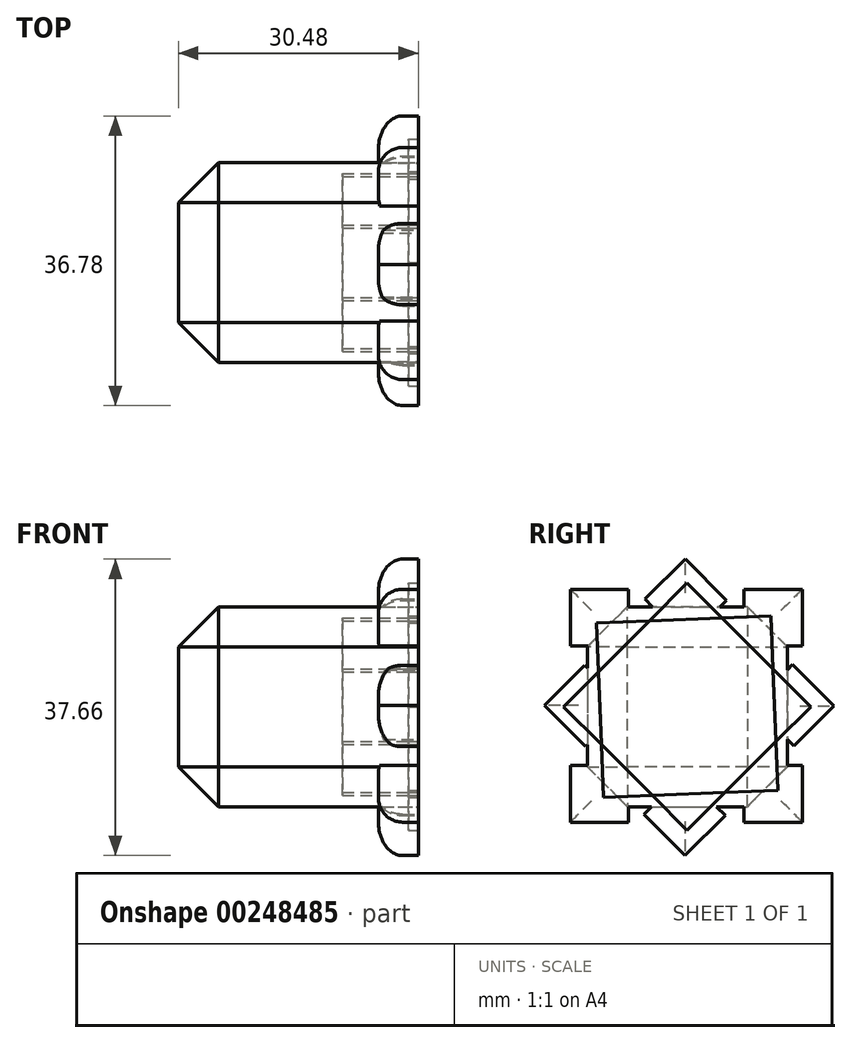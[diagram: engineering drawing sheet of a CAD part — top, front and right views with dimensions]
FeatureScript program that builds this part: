
annotation { "Feature Type Name" : "Feature", "Feature Type Description" : "" }
export const myFeature = defineFeature(function(context is Context, id is Id, definition is map)
    precondition{}
    {
        {
            var Q0;
            Q0=qCreatedBy(makeId("Front.planeOp"),FACE);
            var sketch = newSketch(context, id + "F0", { "sketchPlane" : qUnion([Q0])});
            skLineSegment(sketch, "E0.bottom", {"start": v(12.7, 12.7) * mm, "end": v(-12.7, 12.7) * mm});
            skLineSegment(sketch, "E0.top", {"start": v(12.7, -12.7) * mm, "end": v(-12.7, -12.7) * mm});
            skLineSegment(sketch, "E0.left", {"start": v(12.7, 12.7) * mm, "end": v(12.7, -12.7) * mm});
            skLineSegment(sketch, "E0.right", {"start": v(-12.7, 12.7) * mm, "end": v(-12.7, -12.7) * mm});
            skPoint(sketch, "E0.middle", {"position": v(0, 0) * mm});
            skSolve(sketch);
        }
        {
            var Q0;
            Q0=makeQuery(id+"F0.imprint","IMPRINT",FACE,{"disambiguationData":[TD([[makeQuery(id+"F0.imprint","IMPRINT",EDGE,{"derivedFrom":sQuery(id+"F0.wireOp",EDGE,"E0.bottom")}),1.0]])]});
            extrude(context, id + "F1", {"entities" : qUnion([Q0]), "depth" : 25.4 * mm});
        }
        {
            var Q0;
            Q0=makeQuery(id+"F1.opExtrude","SWEPT_FACE",FACE,{"disambiguationData":[OSD([sQuery(id+"F0.wireOp",EDGE,"E0.left")])]});
            var sketch = newSketch(context, id + "F2", { "sketchPlane" : qUnion([Q0])});
            skLineSegment(sketch, "E1.bottom", {"start": v(-27.56, 7.72) * mm, "end": v(-27.56, 14.93) * mm});
            skLineSegment(sketch, "E1.top", {"start": v(-20.15, 7.72) * mm, "end": v(-20.15, 14.93) * mm});
            skLineSegment(sketch, "E1.left", {"start": v(-27.56, 7.72) * mm, "end": v(-20.15, 7.72) * mm});
            skLineSegment(sketch, "E1.right", {"start": v(-27.56, 14.93) * mm, "end": v(-20.15, 14.93) * mm});
            skLineSegment(sketch, "E2.bottom", {"start": v(-5.5, 7.72) * mm, "end": v(-5.5, 14.93) * mm});
            skLineSegment(sketch, "E2.top", {"start": v(1.9, 7.72) * mm, "end": v(1.9, 14.93) * mm});
            skLineSegment(sketch, "E2.left", {"start": v(-5.5, 7.72) * mm, "end": v(1.9, 7.72) * mm});
            skLineSegment(sketch, "E2.right", {"start": v(-5.5, 14.93) * mm, "end": v(1.9, 14.93) * mm});
            skLineSegment(sketch, "E3.bottom", {"start": v(-5.5, -14.66) * mm, "end": v(-5.5, -7.45) * mm});
            skLineSegment(sketch, "E3.top", {"start": v(1.9, -14.66) * mm, "end": v(1.9, -7.45) * mm});
            skLineSegment(sketch, "E3.left", {"start": v(-5.5, -14.66) * mm, "end": v(1.9, -14.66) * mm});
            skLineSegment(sketch, "E3.right", {"start": v(-5.5, -7.45) * mm, "end": v(1.9, -7.45) * mm});
            skLineSegment(sketch, "E4.bottom", {"start": v(-27.56, -14.66) * mm, "end": v(-27.56, -7.45) * mm});
            skLineSegment(sketch, "E4.left", {"start": v(-27.56, -14.66) * mm, "end": v(-20.15, -14.66) * mm});
            skLineSegment(sketch, "E4.right", {"start": v(-27.56, -7.45) * mm, "end": v(-20.15, -7.45) * mm});
            skPoint(sketch, "E5", {"position": v(-5.5, -11.06) * mm});
            skPoint(sketch, "E6", {"position": v(-23.86, -7.45) * mm});
            skPoint(sketch, "E7", {"position": v(-1.8, -7.45) * mm});
            skPoint(sketch, "E8", {"position": v(-20.15, 11.32) * mm});
            skLineSegment(sketch, "E9", {"start": v(-20.15, -7.45) * mm, "end": v(-20.15, -14.66) * mm});
            skSolve(sketch);
        }
        {
            var Q0;
            {var subQ2=sQuery(id+"F2.wireOp",EDGE,"E1.bottom");Q0=makeQuery(id+"F2.imprint","IMPRINT",FACE,{"disambiguationData":[TD([[makeQuery(id+"F2.imprint","IMPRINT",EDGE,{"derivedFrom":subQ2}),-1.0]])]});}
            var Q1;
            {var subQ0=sQuery(id+"F2.wireOp",EDGE,"E1.left");var subQ1=sQuery(id+"F2.wireOp",EDGE,"E1.top");var subQ2=makeQuery(id+"F2.imprint","INTERSECT",VERTEX,{"derivedFrom":[subQ1,subQ0]});Q1=makeQuery(id+"F2.imprint","IMPRINT",FACE,{"disambiguationData":[TD([[makeQuery(id+"F2.imprint","IMPRINT",EDGE,{"disambiguationData":[TD([[subQ2,1.0]])],"derivedFrom":subQ0}),1.0]])]});}
            var Q2;
            {var subQ0=sQuery(id+"F2.wireOp",EDGE,"E2.left");var subQ1=sQuery(id+"F2.wireOp",EDGE,"E2.bottom");var subQ2=makeQuery(id+"F2.imprint","INTERSECT",VERTEX,{"derivedFrom":[subQ1,subQ0]});Q2=makeQuery(id+"F2.imprint","IMPRINT",FACE,{"disambiguationData":[TD([[makeQuery(id+"F2.imprint","IMPRINT",EDGE,{"disambiguationData":[TD([[subQ2,-1.0]])],"derivedFrom":subQ0}),1.0]])]});}
            var Q3;
            {var subQ7=sQuery(id+"F2.wireOp",EDGE,"E2.top");Q3=makeQuery(id+"F2.imprint","IMPRINT",FACE,{"disambiguationData":[TD([[makeQuery(id+"F2.imprint","IMPRINT",EDGE,{"derivedFrom":subQ7}),1.0]])]});}
            var Q4;
            {var subQ1=sQuery(id+"F2.wireOp",EDGE,"E3.top");Q4=makeQuery(id+"F2.imprint","IMPRINT",FACE,{"disambiguationData":[TD([[makeQuery(id+"F2.imprint","IMPRINT",EDGE,{"derivedFrom":subQ1}),1.0]])]});}
            var Q5;
            {var subQ1=sQuery(id+"F2.wireOp",EDGE,"E4.bottom");Q5=makeQuery(id+"F2.imprint","IMPRINT",FACE,{"disambiguationData":[TD([[makeQuery(id+"F2.imprint","IMPRINT",EDGE,{"derivedFrom":subQ1}),-1.0]])]});}
            var Q6;
            {var subQ0=sQuery(id+"F2.wireOp",EDGE,"E4.right");var subQ1=sQuery(id+"F2.wireOp",EDGE,"E4.top");var subQ2=makeQuery(id+"F2.imprint","INTERSECT",VERTEX,{"derivedFrom":[subQ1,subQ0]});Q6=makeQuery(id+"F2.imprint","IMPRINT",FACE,{"disambiguationData":[TD([[makeQuery(id+"F2.imprint","IMPRINT",EDGE,{"disambiguationData":[TD([[subQ2,1.0]])],"derivedFrom":subQ0}),-1.0]])]});}
            var Q7;
            {var subQ0=sQuery(id+"F2.wireOp",EDGE,"E3.right");var subQ1=sQuery(id+"F2.wireOp",EDGE,"E3.bottom");var subQ2=makeQuery(id+"F2.imprint","INTERSECT",VERTEX,{"derivedFrom":[subQ1,subQ0]});Q7=makeQuery(id+"F2.imprint","IMPRINT",FACE,{"disambiguationData":[TD([[makeQuery(id+"F2.imprint","IMPRINT",EDGE,{"disambiguationData":[TD([[subQ2,-1.0]])],"derivedFrom":subQ0}),-1.0]])]});}
            var Q8;
            Q8=makeQuery(id+"F1.opExtrude","SWEPT_FACE",FACE,{"disambiguationData":[OSD([sQuery(id+"F0.wireOp",EDGE,"E0.left")])]});
            var Q9;
            Q9=makeQuery(id+"F1.opExtrude","SWEPT_FACE",FACE,{"disambiguationData":[OSD([sQuery(id+"F0.wireOp",EDGE,"E0.right")])]});
            extrude(context, id + "F3", {"entities" : qUnion([Q0, Q1, Q2, Q3, Q4, Q5, Q6, Q7, Q8, Q9]), "operationType" : NewBodyOperationType.ADD, "endBound" : BoundingType.SYMMETRIC, "depth" : 5.08 * mm});
        }
        {
            var Q0;
            Q0=makeQuery(id+"F3.boolean.opBoolean","MERGE",FACE,{"derivedFrom":[makeQuery(id+"F3.opExtrude","CAP_FACE",FACE,{"disambiguationData":[OSD([sQuery(id+"F0.wireOp",EDGE,"E0.left")])],"isStart":false}),makeQuery(id+"F3.opExtrude","CAP_FACE",FACE,{"disambiguationData":[OSD([sQuery(id+"F2.wireOp",EDGE,"E1.bottom"),sQuery(id+"F2.wireOp",EDGE,"E1.top"),sQuery(id+"F2.wireOp",EDGE,"E1.left"),sQuery(id+"F2.wireOp",EDGE,"E1.right")])],"isStart":false}),makeQuery(id+"F3.opExtrude","CAP_FACE",FACE,{"disambiguationData":[OSD([sQuery(id+"F2.wireOp",EDGE,"E2.bottom"),sQuery(id+"F2.wireOp",EDGE,"E2.top"),sQuery(id+"F2.wireOp",EDGE,"E2.left"),sQuery(id+"F2.wireOp",EDGE,"E2.right")])],"isStart":false}),makeQuery(id+"F3.opExtrude","CAP_FACE",FACE,{"disambiguationData":[OSD([sQuery(id+"F2.wireOp",EDGE,"E3.bottom"),sQuery(id+"F2.wireOp",EDGE,"E3.top"),sQuery(id+"F2.wireOp",EDGE,"E3.left"),sQuery(id+"F2.wireOp",EDGE,"E3.right")])],"isStart":false}),makeQuery(id+"F3.opExtrude","CAP_FACE",FACE,{"disambiguationData":[OSD([sQuery(id+"F2.wireOp",EDGE,"E4.bottom"),sQuery(id+"F2.wireOp",EDGE,"E4.left"),sQuery(id+"F2.wireOp",EDGE,"E4.right"),sQuery(id+"F2.wireOp",EDGE,"E9")])],"isStart":false})]});
            var sketch = newSketch(context, id + "F4", { "sketchPlane" : qUnion([Q0])});
            skLineSegment(sketch, "E10.bottom", {"start": v(-18.07, 13.67) * mm, "end": v(-12.97, 18.76) * mm});
            skLineSegment(sketch, "E10.top", {"start": v(-12.83, 8.43) * mm, "end": v(-7.73, 13.52) * mm});
            skLineSegment(sketch, "E10.left", {"start": v(-18.07, 13.67) * mm, "end": v(-12.83, 8.43) * mm});
            skLineSegment(sketch, "E10.right", {"start": v(-12.97, 18.76) * mm, "end": v(-7.73, 13.52) * mm});
            skLineSegment(sketch, "E11.bottom", {"start": v(-4.43, 0.25) * mm, "end": v(0.67, 5.35) * mm});
            skLineSegment(sketch, "E11.top", {"start": v(0.81, -5) * mm, "end": v(5.91, 0.1) * mm});
            skLineSegment(sketch, "E11.left", {"start": v(-4.43, 0.25) * mm, "end": v(0.81, -5) * mm});
            skLineSegment(sketch, "E11.right", {"start": v(0.67, 5.35) * mm, "end": v(5.91, 0.1) * mm});
            skLineSegment(sketch, "E12.bottom", {"start": v(-18.22, -13.66) * mm, "end": v(-13.12, -8.56) * mm});
            skLineSegment(sketch, "E12.top", {"start": v(-12.98, -18.9) * mm, "end": v(-7.88, -13.8) * mm});
            skLineSegment(sketch, "E12.left", {"start": v(-18.22, -13.66) * mm, "end": v(-12.98, -18.9) * mm});
            skLineSegment(sketch, "E12.right", {"start": v(-13.12, -8.56) * mm, "end": v(-7.88, -13.8) * mm});
            skLineSegment(sketch, "E13.bottom", {"start": v(-30.87, 0.17) * mm, "end": v(-25.77, 5.27) * mm});
            skLineSegment(sketch, "E13.left", {"start": v(-30.87, 0.17) * mm, "end": v(-25.63, -5.07) * mm});
            skLineSegment(sketch, "E13.right", {"start": v(-25.77, 5.27) * mm, "end": v(-20.53, 0.03) * mm});
            skPoint(sketch, "E14", {"position": v(-15.67, -11.11) * mm});
            skPoint(sketch, "E15", {"position": v(-23.15, 2.65) * mm});
            skPoint(sketch, "E16", {"position": v(-10.5, -11.18) * mm});
            skPoint(sketch, "E17", {"position": v(-10.28, 10.98) * mm});
            skLineSegment(sketch, "E18", {"start": v(-20.53, 0.03) * mm, "end": v(-25.63, -5.07) * mm});
            skSolve(sketch);
        }
        {
            var Q0;
            {var subQ2=sQuery(id+"F4.wireOp",EDGE,"E10.bottom");Q0=makeQuery(id+"F4.imprint","IMPRINT",FACE,{"disambiguationData":[TD([[makeQuery(id+"F4.imprint","IMPRINT",EDGE,{"derivedFrom":subQ2}),-1.0]])]});}
            var Q1;
            {var subQ2=sQuery(id+"F4.wireOp",EDGE,"E11.top");Q1=makeQuery(id+"F4.imprint","IMPRINT",FACE,{"disambiguationData":[TD([[makeQuery(id+"F4.imprint","IMPRINT",EDGE,{"derivedFrom":subQ2}),1.0]])]});}
            var Q2;
            {var subQ1=sQuery(id+"F4.wireOp",EDGE,"E12.top");Q2=makeQuery(id+"F4.imprint","IMPRINT",FACE,{"disambiguationData":[TD([[makeQuery(id+"F4.imprint","IMPRINT",EDGE,{"derivedFrom":subQ1}),1.0]])]});}
            var Q3;
            {var subQ6=sQuery(id+"F4.wireOp",EDGE,"E13.bottom");Q3=makeQuery(id+"F4.imprint","IMPRINT",FACE,{"disambiguationData":[TD([[makeQuery(id+"F4.imprint","IMPRINT",EDGE,{"derivedFrom":subQ6}),-1.0]])]});}
            extrude(context, id + "F5", {"entities" : qUnion([Q0, Q1, Q2, Q3]), "operationType" : NewBodyOperationType.ADD, "oppositeDirection" : true, "depth" : 5.08 * mm});
        }
        {
            var Q0;
            Q0=makeQuery(id+"F3.opExtrude","CAP_EDGE",EDGE,{"disambiguationData":[OSD([sQuery(id+"F0.wireOp",EDGE,"E0.top"),sQuery(id+"F0.wireOp",EDGE,"E0.right")])],"isStart":true});
            var Q1;
            Q1=makeQuery(id+"F3.opExtrude","CAP_FACE",FACE,{"disambiguationData":[OSD([sQuery(id+"F0.wireOp",EDGE,"E0.right")])],"isStart":true});
            var Q2;
            {var subQ0=sQuery(id+"F0.wireOp",EDGE,"E0.right");var subQ1=sQuery(id+"F0.wireOp",EDGE,"E0.bottom");Q2=makeQuery(id+"F3.boolean.opBoolean","MERGE",EDGE,{"derivedFrom":[makeQuery(id+"F1.opExtrude","CAP_EDGE",EDGE,{"disambiguationData":[OSD([subQ1])],"isStart":false}),makeQuery(id+"F3.opExtrude","SWEPT_EDGE",EDGE,{"disambiguationData":[OSD([subQ1,subQ0]),TDD([makeQuery(id+"F1.opExtrude","CAP_VERTEX",VERTEX,{"disambiguationData":[OSD([subQ1,subQ0])],"isStart":false})])]})]});}
            var Q3;
            {var subQ0=sQuery(id+"F0.wireOp",EDGE,"E0.right");var subQ1=sQuery(id+"F0.wireOp",EDGE,"E0.top");Q3=makeQuery(id+"F3.boolean.opBoolean","MERGE",EDGE,{"derivedFrom":[makeQuery(id+"F1.opExtrude","CAP_EDGE",EDGE,{"disambiguationData":[OSD([subQ1])],"isStart":false}),makeQuery(id+"F3.opExtrude","SWEPT_EDGE",EDGE,{"disambiguationData":[OSD([subQ1,subQ0]),TDD([makeQuery(id+"F1.opExtrude","CAP_VERTEX",VERTEX,{"disambiguationData":[OSD([subQ1,subQ0])],"isStart":false})])]})]});}
            var Q4;
            {var subQ0=sQuery(id+"F0.wireOp",EDGE,"E0.right");var subQ1=sQuery(id+"F0.wireOp",EDGE,"E0.top");Q4=makeQuery(id+"F3.boolean.opBoolean","MERGE",EDGE,{"derivedFrom":[makeQuery(id+"F1.opExtrude","CAP_EDGE",EDGE,{"disambiguationData":[OSD([subQ1])],"isStart":true}),makeQuery(id+"F3.opExtrude","SWEPT_EDGE",EDGE,{"disambiguationData":[OSD([subQ1,subQ0]),TDD([makeQuery(id+"F1.opExtrude","CAP_VERTEX",VERTEX,{"disambiguationData":[OSD([subQ1,subQ0])],"isStart":true})])]})]});}
            var Q5;
            {var subQ0=sQuery(id+"F0.wireOp",EDGE,"E0.right");var subQ1=sQuery(id+"F0.wireOp",EDGE,"E0.bottom");Q5=makeQuery(id+"F3.boolean.opBoolean","MERGE",EDGE,{"derivedFrom":[makeQuery(id+"F1.opExtrude","CAP_EDGE",EDGE,{"disambiguationData":[OSD([subQ1])],"isStart":true}),makeQuery(id+"F3.opExtrude","SWEPT_EDGE",EDGE,{"disambiguationData":[OSD([subQ1,subQ0]),TDD([makeQuery(id+"F1.opExtrude","CAP_VERTEX",VERTEX,{"disambiguationData":[OSD([subQ1,subQ0])],"isStart":true})])]})]});}
            chamfer(context, id + "F6", {"entities" : qUnion([Q0, Q1, Q2, Q3, Q4, Q5]), "width" : 5.08 * mm, "tangentPropagation" : true});
        }
        {
            var Q0;
            Q0=makeQuery(id+"F5.opExtrude","CAP_EDGE",EDGE,{"disambiguationData":[OSD([sQuery(id+"F4.wireOp",EDGE,"E12.left")])],"isStart":false});
            var Q1;
            Q1=makeQuery(id+"F5.opExtrude","CAP_EDGE",EDGE,{"disambiguationData":[OSD([sQuery(id+"F4.wireOp",EDGE,"E12.top")])],"isStart":false});
            var Q2;
            Q2=makeQuery(id+"F3.opExtrude","CAP_EDGE",EDGE,{"disambiguationData":[OSD([sQuery(id+"F2.wireOp",EDGE,"E3.left")])],"isStart":true});
            var Q3;
            Q3=makeQuery(id+"F3.opExtrude","CAP_EDGE",EDGE,{"disambiguationData":[OSD([sQuery(id+"F2.wireOp",EDGE,"E3.top")])],"isStart":true});
            var Q4;
            Q4=makeQuery(id+"F3.opExtrude","CAP_EDGE",EDGE,{"disambiguationData":[OSD([sQuery(id+"F2.wireOp",EDGE,"E4.left")])],"isStart":true});
            var Q5;
            Q5=makeQuery(id+"F3.opExtrude","CAP_EDGE",EDGE,{"disambiguationData":[OSD([sQuery(id+"F2.wireOp",EDGE,"E4.bottom")])],"isStart":true});
            var Q6;
            Q6=makeQuery(id+"F5.opExtrude","CAP_EDGE",EDGE,{"disambiguationData":[OSD([sQuery(id+"F4.wireOp",EDGE,"E13.left")])],"isStart":false});
            var Q7;
            Q7=makeQuery(id+"F5.opExtrude","CAP_EDGE",EDGE,{"disambiguationData":[OSD([sQuery(id+"F4.wireOp",EDGE,"E13.bottom")])],"isStart":false});
            var Q8;
            Q8=makeQuery(id+"F3.opExtrude","CAP_EDGE",EDGE,{"disambiguationData":[OSD([sQuery(id+"F2.wireOp",EDGE,"E1.bottom")])],"isStart":true});
            var Q9;
            Q9=makeQuery(id+"F3.opExtrude","CAP_EDGE",EDGE,{"disambiguationData":[OSD([sQuery(id+"F2.wireOp",EDGE,"E1.right")])],"isStart":true});
            var Q10;
            Q10=makeQuery(id+"F5.opExtrude","CAP_EDGE",EDGE,{"disambiguationData":[OSD([sQuery(id+"F4.wireOp",EDGE,"E11.top")])],"isStart":false});
            var Q11;
            Q11=makeQuery(id+"F5.opExtrude","CAP_EDGE",EDGE,{"disambiguationData":[OSD([sQuery(id+"F4.wireOp",EDGE,"E11.right")])],"isStart":false});
            var Q12;
            Q12=makeQuery(id+"F3.opExtrude","CAP_EDGE",EDGE,{"disambiguationData":[OSD([sQuery(id+"F2.wireOp",EDGE,"E2.top")])],"isStart":true});
            var Q13;
            Q13=makeQuery(id+"F3.opExtrude","CAP_EDGE",EDGE,{"disambiguationData":[OSD([sQuery(id+"F2.wireOp",EDGE,"E2.right")])],"isStart":true});
            var Q14;
            Q14=makeQuery(id+"F5.opExtrude","CAP_EDGE",EDGE,{"disambiguationData":[OSD([sQuery(id+"F4.wireOp",EDGE,"E10.right")])],"isStart":false});
            var Q15;
            Q15=makeQuery(id+"F5.opExtrude","CAP_EDGE",EDGE,{"disambiguationData":[OSD([sQuery(id+"F4.wireOp",EDGE,"E10.bottom")])],"isStart":false});
            fillet(context, id + "F7", {"entities" : qUnion([Q0, Q1, Q2, Q3, Q4, Q5, Q6, Q7, Q8, Q9, Q10, Q11, Q12, Q13, Q14, Q15]), "radius" : 3.07 * mm, "tangentPropagation" : true, "allowEdgeOverflow" : false});
        }
        {
            var Q0;
            {var subQ0=sQuery(id+"F0.wireOp",EDGE,"E0.left");Q0=makeQuery(id+"F5.boolean.opBoolean","MERGE",FACE,{"derivedFrom":[makeQuery(id+"F3.boolean.opBoolean","MERGE",FACE,{"derivedFrom":[makeQuery(id+"F3.opExtrude","CAP_FACE",FACE,{"disambiguationData":[OSD([subQ0])],"isStart":false}),makeQuery(id+"F3.opExtrude","CAP_FACE",FACE,{"disambiguationData":[OSD([sQuery(id+"F2.wireOp",EDGE,"E1.bottom"),sQuery(id+"F2.wireOp",EDGE,"E1.top"),sQuery(id+"F2.wireOp",EDGE,"E1.left"),sQuery(id+"F2.wireOp",EDGE,"E1.right")])],"isStart":false}),makeQuery(id+"F3.opExtrude","CAP_FACE",FACE,{"disambiguationData":[OSD([sQuery(id+"F2.wireOp",EDGE,"E2.bottom"),sQuery(id+"F2.wireOp",EDGE,"E2.top"),sQuery(id+"F2.wireOp",EDGE,"E2.left"),sQuery(id+"F2.wireOp",EDGE,"E2.right")])],"isStart":false}),makeQuery(id+"F3.opExtrude","CAP_FACE",FACE,{"disambiguationData":[OSD([sQuery(id+"F2.wireOp",EDGE,"E3.bottom"),sQuery(id+"F2.wireOp",EDGE,"E3.top"),sQuery(id+"F2.wireOp",EDGE,"E3.left"),sQuery(id+"F2.wireOp",EDGE,"E3.right")])],"isStart":false}),makeQuery(id+"F3.opExtrude","CAP_FACE",FACE,{"disambiguationData":[OSD([sQuery(id+"F2.wireOp",EDGE,"E4.bottom"),sQuery(id+"F2.wireOp",EDGE,"E4.left"),sQuery(id+"F2.wireOp",EDGE,"E4.right"),sQuery(id+"F2.wireOp",EDGE,"E9")])],"isStart":false})]}),makeQuery(id+"F5.opExtrude","CAP_FACE",FACE,{"disambiguationData":[OSD([sQuery(id+"F0.wireOp",EDGE,"E0.bottom"),subQ0,sQuery(id+"F4.wireOp",EDGE,"E10.bottom"),sQuery(id+"F4.wireOp",EDGE,"E10.top"),sQuery(id+"F4.wireOp",EDGE,"E10.left"),sQuery(id+"F4.wireOp",EDGE,"E10.right")])],"isStart":true}),makeQuery(id+"F5.opExtrude","CAP_FACE",FACE,{"disambiguationData":[OSD([subQ0,sQuery(id+"F4.wireOp",EDGE,"E11.bottom"),sQuery(id+"F4.wireOp",EDGE,"E11.top"),sQuery(id+"F4.wireOp",EDGE,"E11.left"),sQuery(id+"F4.wireOp",EDGE,"E11.right")])],"isStart":true}),makeQuery(id+"F5.opExtrude","CAP_FACE",FACE,{"disambiguationData":[OSD([sQuery(id+"F0.wireOp",EDGE,"E0.top"),subQ0,sQuery(id+"F4.wireOp",EDGE,"E12.bottom"),sQuery(id+"F4.wireOp",EDGE,"E12.top"),sQuery(id+"F4.wireOp",EDGE,"E12.left"),sQuery(id+"F4.wireOp",EDGE,"E12.right")])],"isStart":true}),makeQuery(id+"F5.opExtrude","CAP_FACE",FACE,{"disambiguationData":[OSD([subQ0,sQuery(id+"F4.wireOp",EDGE,"E13.bottom"),sQuery(id+"F4.wireOp",EDGE,"E13.left"),sQuery(id+"F4.wireOp",EDGE,"E13.right"),sQuery(id+"F4.wireOp",EDGE,"E18")])],"isStart":true})]});}
            var sketch = newSketch(context, id + "F8", { "sketchPlane" : qUnion([Q0])});
            skCircle(sketch, "E19.cCircle", {"center": v(-12.72, 0) * mm, "radius": 15.7 * mm, "construction": true});
            skLineSegment(sketch, "E19.0", {"start": v(2.98, 0) * mm, "end": v(-12.72, -15.7) * mm});
            skLineSegment(sketch, "E19.1", {"start": v(-12.72, -15.7) * mm, "end": v(-28.42, 0) * mm});
            skLineSegment(sketch, "E19.2", {"start": v(-28.42, 0) * mm, "end": v(-12.72, 15.7) * mm});
            skLineSegment(sketch, "E19.3", {"start": v(-12.72, 15.7) * mm, "end": v(2.98, 0) * mm});
            skLineSegment(sketch, "E20.0", {"start": v(-2.09, 11.55) * mm, "end": v(-1.17, -10.63) * mm});
            skLineSegment(sketch, "E20.1", {"start": v(-1.17, -10.63) * mm, "end": v(-23.35, -11.55) * mm});
            skLineSegment(sketch, "E20.2", {"start": v(-23.35, -11.55) * mm, "end": v(-24.27, 10.63) * mm});
            skLineSegment(sketch, "E20.3", {"start": v(-24.27, 10.63) * mm, "end": v(-2.09, 11.55) * mm});
            skPoint(sketch, "E21", {"position": v(-17.5, 10.91) * mm});
            skPoint(sketch, "E22", {"position": v(-8.31, 11.3) * mm});
            skPoint(sketch, "E23", {"position": v(-1.8, 4.79) * mm});
            skPoint(sketch, "E24", {"position": v(-1.43, -4.4) * mm});
            skPoint(sketch, "E25", {"position": v(-7.94, -10.91) * mm});
            skPoint(sketch, "E26", {"position": v(-17.13, -11.3) * mm});
            skPoint(sketch, "E27", {"position": v(-23.63, -4.79) * mm});
            skPoint(sketch, "E28", {"position": v(-24.01, 4.4) * mm});
            skSolve(sketch);
        }
        {
            var Q0;
            Q0 = qSketchRegion(id + "F8", true);
            extrude(context, id + "F9", {"entities" : qUnion([Q0]), "operationType" : NewBodyOperationType.REMOVE, "oppositeDirection" : true, "depth" : 1.27 * mm});
        }
        {
            var Q0;
            {var subQ11=sQuery(id+"F8.wireOp",EDGE,"E20.0");var subQ13=sQuery(id+"F8.wireOp",EDGE,"E19.0");var subQ14=makeQuery(id+"F8.imprint","INTERSECT",VERTEX,{"derivedFrom":[subQ13,subQ11]});Q0=makeQuery(id+"F8.imprint","IMPRINT",FACE,{"disambiguationData":[TD([[makeQuery(id+"F8.imprint","IMPRINT",EDGE,{"disambiguationData":[TD([[subQ14,-1.0]])],"derivedFrom":subQ13}),-1.0]])]});}
            extrude(context, id + "F10", {"entities" : qUnion([Q0]), "oppositeDirection" : true, "depth" : 9.65 * mm});
        }
    });
